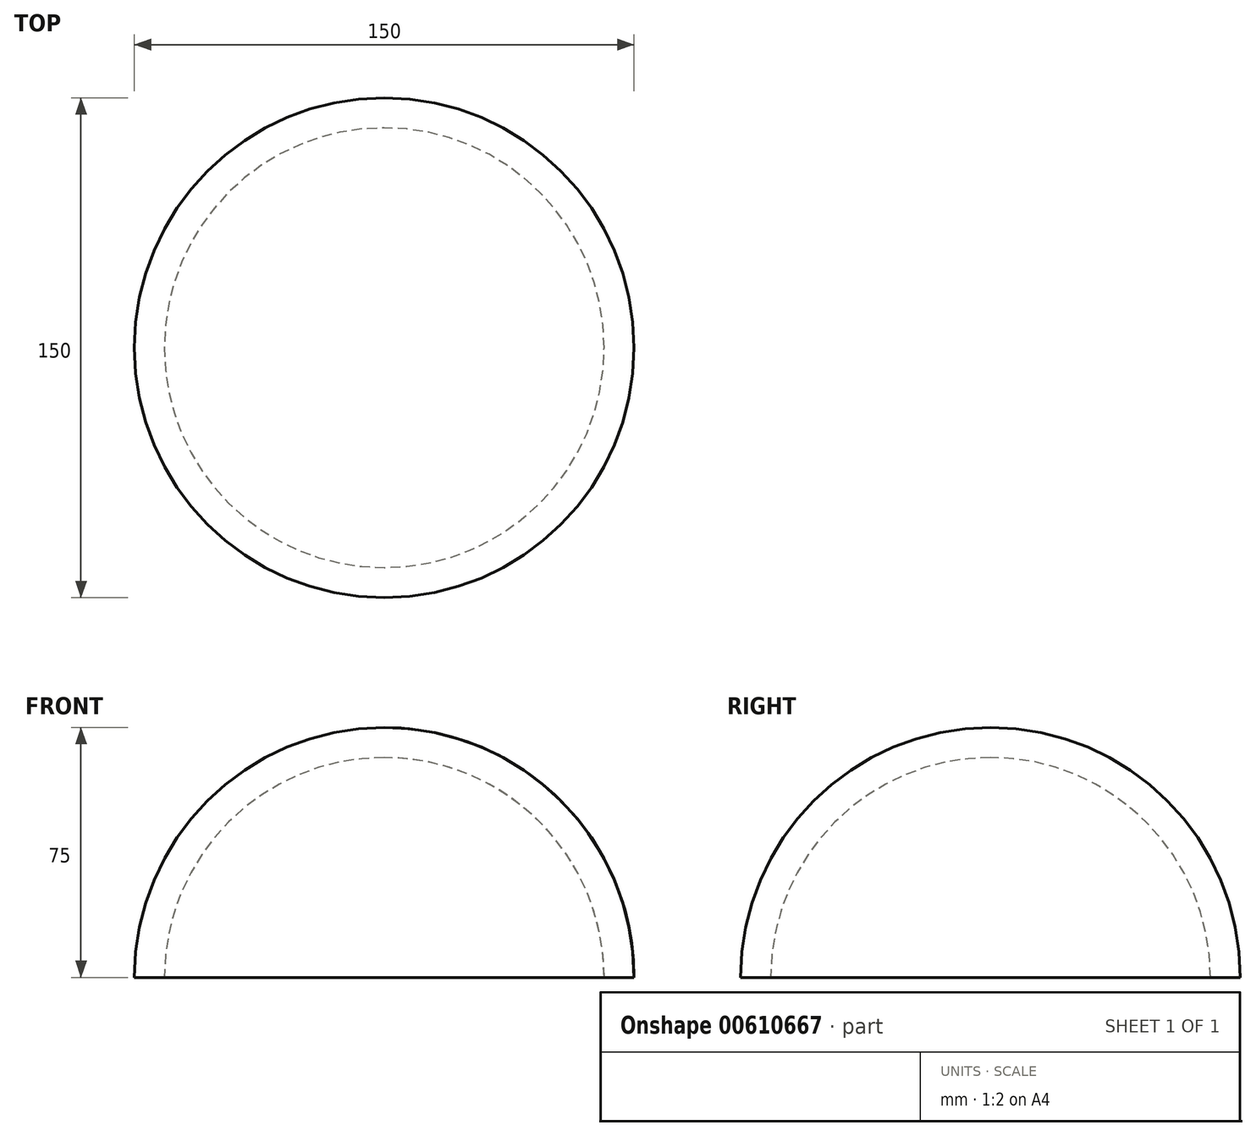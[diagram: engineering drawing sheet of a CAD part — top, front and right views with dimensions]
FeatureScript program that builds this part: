
annotation { "Feature Type Name" : "Feature", "Feature Type Description" : "" }
export const myFeature = defineFeature(function(context is Context, id is Id, definition is map)
    precondition{}
    {
        {
            var Q0;
            Q0=qCreatedBy(makeId("Front.planeOp"),FACE);
            var sketch = newSketch(context, id + "F0", { "sketchPlane" : qUnion([Q0])});
            skCircle(sketch, "E0", {"center": v(0, 0) * mm, "radius": 75 * mm});
            skLineSegment(sketch, "E1", {"start": v(-77.91, 0) * mm, "end": v(82.69, 0) * mm});
            skLineSegment(sketch, "E2", {"start": v(0, 84.11) * mm, "end": v(0, -81.35) * mm});
            skCircle(sketch, "E3", {"center": v(0, 0) * mm, "radius": 66 * mm});
            skSolve(sketch);
        }
        {
            var Q0;
            {var subQ0=sQuery(id+"F0.wireOp",EDGE,"E1");var subQ1=sQuery(id+"F0.wireOp",EDGE,"E0");var subQ2=makeQuery(id+"F0.imprint","INTERSECT",VERTEX,{"disambiguationData":[OD(1.0)],"derivedFrom":[subQ1,subQ0]});Q0=makeQuery(id+"F0.imprint","IMPRINT",FACE,{"disambiguationData":[TD([[makeQuery(id+"F0.imprint","IMPRINT",EDGE,{"disambiguationData":[TD([[subQ2,-1.0]])],"derivedFrom":subQ1}),1.0]])]});}
            var Q1;
            Q1=sQuery(id+"F0.wireOp",EDGE,"E2");
            revolve(context, id + "F1", {"entities" : qUnion([Q0]), "axis" : qUnion([Q1]), "revolveType" : RevolveType.FULL});
        }
    });
